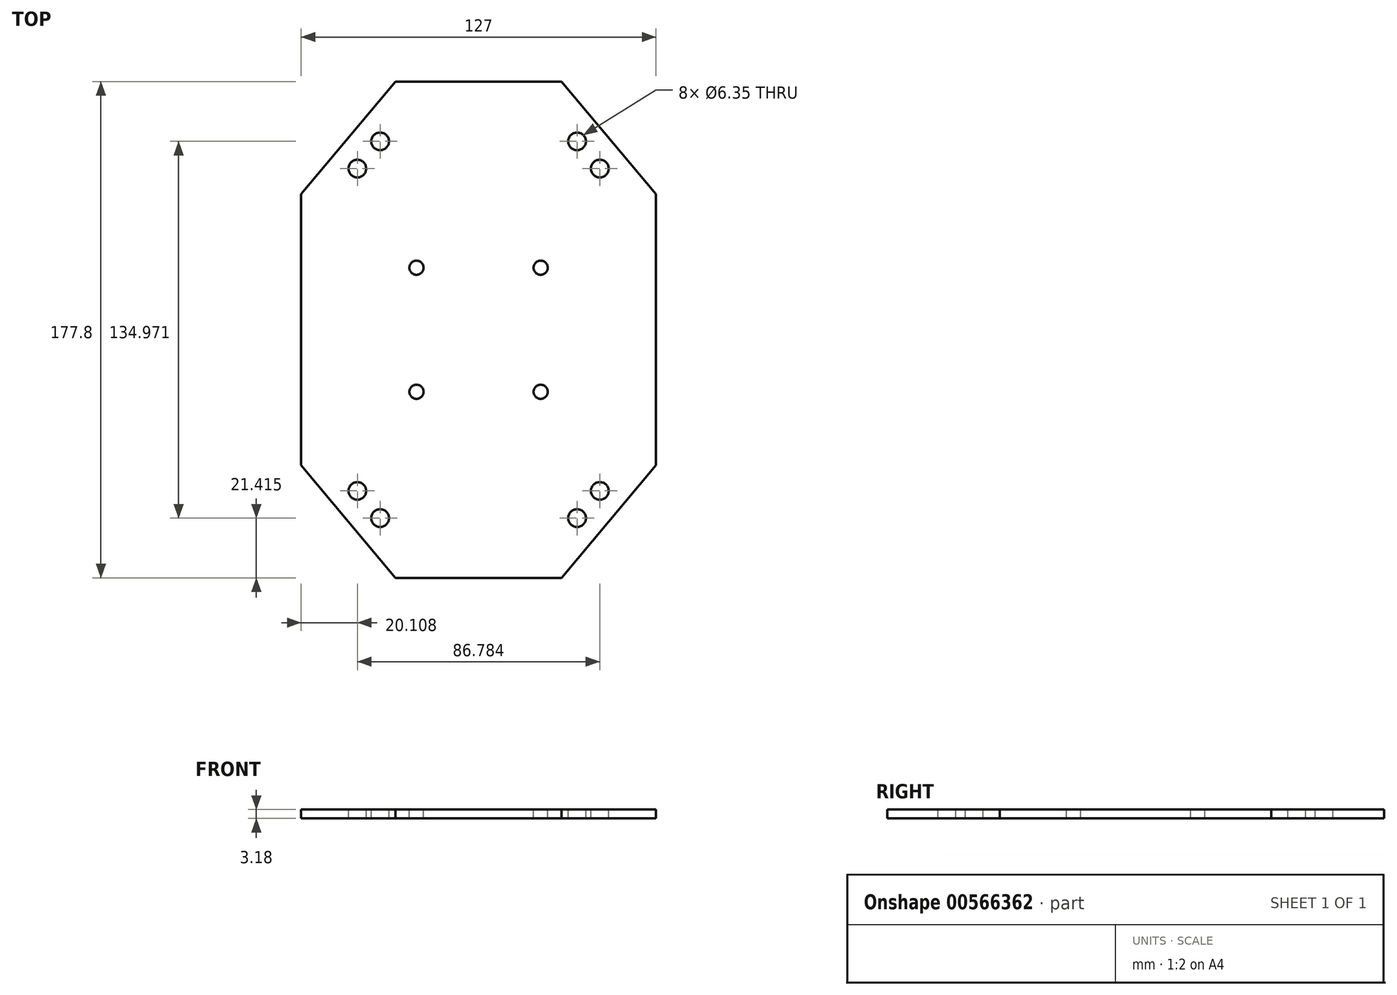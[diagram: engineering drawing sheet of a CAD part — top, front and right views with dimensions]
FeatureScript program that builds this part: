
annotation { "Feature Type Name" : "Feature", "Feature Type Description" : "" }
export const myFeature = defineFeature(function(context is Context, id is Id, definition is map)
    precondition{}
    {
        {
            var Q0;
            Q0=qCreatedBy(makeId("Top.planeOp"),FACE);
            var sketch = newSketch(context, id + "F0", { "sketchPlane" : qUnion([Q0])});
            skLineSegment(sketch, "E0", {"start": v(-29.75, 88.9) * mm, "end": v(29.75, 88.9) * mm});
            skLineSegment(sketch, "E1", {"start": v(29.75, 88.9) * mm, "end": v(63.5, 48.55) * mm});
            skLineSegment(sketch, "E2", {"start": v(63.5, 48.55) * mm, "end": v(63.5, -48.55) * mm});
            skLineSegment(sketch, "E3", {"start": v(63.5, -48.55) * mm, "end": v(29.75, -88.9) * mm});
            skLineSegment(sketch, "E4", {"start": v(29.75, -88.9) * mm, "end": v(-29.75, -88.9) * mm});
            skLineSegment(sketch, "E5", {"start": v(-29.75, -88.9) * mm, "end": v(-63.5, -48.55) * mm});
            skLineSegment(sketch, "E6", {"start": v(-63.5, -48.55) * mm, "end": v(-63.5, 48.55) * mm});
            skLineSegment(sketch, "E7", {"start": v(-63.5, 48.55) * mm, "end": v(-29.75, 88.9) * mm});
            skSolve(sketch);
        }
        {
            var Q0;
            Q0=makeQuery(id+"F0.imprint","IMPRINT",FACE,{"disambiguationData":[TD([[makeQuery(id+"F0.imprint","IMPRINT",EDGE,{"derivedFrom":sQuery(id+"F0.wireOp",EDGE,"E0")}),-1.0]])]});
            extrude(context, id + "F1", {"entities" : qUnion([Q0]), "depth" : 3.17 * mm, "offsetDistance" : 25.4 * mm});
        }
        {
            var Q0;
            Q0=makeQuery(id+"F1.opExtrude","CAP_FACE",FACE,{"disambiguationData":[OSD([sQuery(id+"F0.wireOp",EDGE,"E0"),sQuery(id+"F0.wireOp",EDGE,"E1"),sQuery(id+"F0.wireOp",EDGE,"E2"),sQuery(id+"F0.wireOp",EDGE,"E3"),sQuery(id+"F0.wireOp",EDGE,"E4"),sQuery(id+"F0.wireOp",EDGE,"E5"),sQuery(id+"F0.wireOp",EDGE,"E6"),sQuery(id+"F0.wireOp",EDGE,"E7")])],"isStart":false});
            var sketch = newSketch(context, id + "F2", { "sketchPlane" : qUnion([Q0])});
            skCircle(sketch, "E8", {"center": v(-43.4, 57.74) * mm, "radius": 3.18 * mm});
            skCircle(sketch, "E9", {"center": v(-35.24, 67.49) * mm, "radius": 3.18 * mm});
            skCircle(sketch, "E10", {"center": v(35.24, 67.49) * mm, "radius": 3.18 * mm});
            skCircle(sketch, "E11", {"center": v(43.4, 57.74) * mm, "radius": 3.18 * mm});
            skCircle(sketch, "E12", {"center": v(35.24, -67.49) * mm, "radius": 3.18 * mm});
            skCircle(sketch, "E13", {"center": v(43.4, -57.74) * mm, "radius": 3.18 * mm});
            skCircle(sketch, "E14", {"center": v(-35.24, -67.49) * mm, "radius": 3.18 * mm});
            skCircle(sketch, "E15", {"center": v(-43.4, -57.74) * mm, "radius": 3.18 * mm});
            skSolve(sketch);
        }
        {
            var Q0;
            Q0=makeQuery(id+"F2.imprint","IMPRINT",FACE,{"disambiguationData":[TD([[makeQuery(id+"F2.imprint","IMPRINT",EDGE,{"derivedFrom":sQuery(id+"F2.wireOp",EDGE,"E8")}),1.0]])]});
            var Q1;
            Q1=makeQuery(id+"F2.imprint","IMPRINT",FACE,{"disambiguationData":[TD([[makeQuery(id+"F2.imprint","IMPRINT",EDGE,{"derivedFrom":sQuery(id+"F2.wireOp",EDGE,"E9")}),1.0]])]});
            var Q2;
            Q2=makeQuery(id+"F2.imprint","IMPRINT",FACE,{"disambiguationData":[TD([[makeQuery(id+"F2.imprint","IMPRINT",EDGE,{"derivedFrom":sQuery(id+"F2.wireOp",EDGE,"E10")}),1.0]])]});
            var Q3;
            Q3=makeQuery(id+"F2.imprint","IMPRINT",FACE,{"disambiguationData":[TD([[makeQuery(id+"F2.imprint","IMPRINT",EDGE,{"derivedFrom":sQuery(id+"F2.wireOp",EDGE,"E11")}),1.0]])]});
            var Q4;
            Q4=makeQuery(id+"F2.imprint","IMPRINT",FACE,{"disambiguationData":[TD([[makeQuery(id+"F2.imprint","IMPRINT",EDGE,{"derivedFrom":sQuery(id+"F2.wireOp",EDGE,"E13")}),1.0]])]});
            var Q5;
            Q5=makeQuery(id+"F2.imprint","IMPRINT",FACE,{"disambiguationData":[TD([[makeQuery(id+"F2.imprint","IMPRINT",EDGE,{"derivedFrom":sQuery(id+"F2.wireOp",EDGE,"E12")}),1.0]])]});
            var Q6;
            Q6=makeQuery(id+"F2.imprint","IMPRINT",FACE,{"disambiguationData":[TD([[makeQuery(id+"F2.imprint","IMPRINT",EDGE,{"derivedFrom":sQuery(id+"F2.wireOp",EDGE,"E14")}),1.0]])]});
            var Q7;
            Q7=makeQuery(id+"F2.imprint","IMPRINT",FACE,{"disambiguationData":[TD([[makeQuery(id+"F2.imprint","IMPRINT",EDGE,{"derivedFrom":sQuery(id+"F2.wireOp",EDGE,"E15")}),1.0]])]});
            extrude(context, id + "F3", {"entities" : qUnion([Q0, Q1, Q2, Q3, Q4, Q5, Q6, Q7]), "operationType" : NewBodyOperationType.REMOVE, "oppositeDirection" : true, "depth" : 25.4 * mm, "offsetDistance" : 25.4 * mm});
        }
        {
            var Q0;
            Q0=makeQuery(id+"F1.opExtrude","CAP_FACE",FACE,{"disambiguationData":[OSD([sQuery(id+"F0.wireOp",EDGE,"E0"),sQuery(id+"F0.wireOp",EDGE,"E1"),sQuery(id+"F0.wireOp",EDGE,"E2"),sQuery(id+"F0.wireOp",EDGE,"E3"),sQuery(id+"F0.wireOp",EDGE,"E4"),sQuery(id+"F0.wireOp",EDGE,"E5"),sQuery(id+"F0.wireOp",EDGE,"E6"),sQuery(id+"F0.wireOp",EDGE,"E7")])],"isStart":false});
            var sketch = newSketch(context, id + "F4", { "sketchPlane" : qUnion([Q0])});
            skCircle(sketch, "E16", {"center": v(-22.23, 22.23) * mm, "radius": 2.54 * mm});
            skCircle(sketch, "E17", {"center": v(22.22, 22.23) * mm, "radius": 2.54 * mm});
            skCircle(sketch, "E18", {"center": v(-22.22, -22.22) * mm, "radius": 2.54 * mm});
            skCircle(sketch, "E19", {"center": v(22.23, -22.23) * mm, "radius": 2.54 * mm});
            skSolve(sketch);
        }
        {
            var Q0;
            Q0=qSketchRegion(id+"F4",true);
            extrude(context, id + "F5", {"entities" : qUnion([Q0]), "operationType" : NewBodyOperationType.REMOVE, "endBound" : BoundingType.THROUGH_ALL, "oppositeDirection" : true, "depth" : 25.4 * mm, "offsetDistance" : 25.4 * mm});
        }
    });
